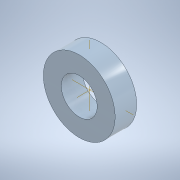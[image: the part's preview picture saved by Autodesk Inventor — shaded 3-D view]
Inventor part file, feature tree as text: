
AUTODESK INVENTOR PART (.ipt)
format: ipt  version: 2021.1 (Build 251245000, 245)  size: 103,424 bytes
history: native  units: in
note: dims shown in document units (in); Inventor stores cm internally (conversion verified against a paired STEP export)
features: extrude x1, sketch x1
ambient origin geometry x8: Origin, YZ Plane, XZ Plane, XY Plane, X Axis, Y Axis, Z Axis, Center Point
bodies: Solid1 (feature_tree)
feature tree (2):
  extrude  "Extrusion1"  Depth=0.3543in
  sketch  "Sketch1"  dims[d0=1.1811in d1=2.3622in d2=0.3543in d3=0.3543in d4=0.0in d5=0.0in]
